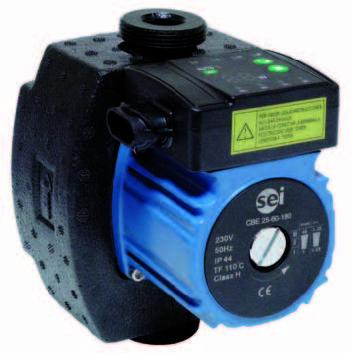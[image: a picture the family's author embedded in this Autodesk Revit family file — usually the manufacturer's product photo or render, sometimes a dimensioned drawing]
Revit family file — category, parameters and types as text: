
# Revit family: CBE_25-60_130-AC52101
name_source: partatom
category: Aparatos eléctricos
revit_build: Autodesk Revit 2016 (Build: 20150220_1215(x64)
units: mm (PartAtom-declared; Revit-internal decimal feet)

## family parameters
Compartido = No
Corte con vacíos al cargar = No
Cota de conector redondo = Diámetro de uso
Mantener orientación de anotación = No
Número OmniClass = 23.80.00.00
Punto de cálculo de habitación = No
Se basa en plano de trabajo = No
Siempre vertical = Sí
Tipo de pieza = Caja de conexiones
Título OmniClass = Electric Power and Lighting

## types (2) — shared parameters
Fabricante = SALVADOR ESCODA
Protección = 6,35 mm (1/4")
URL = www.salvadorescoda.com
zero-valued in all types: Costo

## per-type parameters (varying)
| type | Aislamiento | Caudal | Conexión rácores | Código de montaje | Descripción | Dimensiones Unidad Interior | Imagen de tipo | Modelo | Motor | Máx. presión trabajo | Peso | Presión disponible | Rango temperatura agua | Temperatura ambiente |
| MVD-22T2 | 35 dB(A) |  |  | CL23370 | CONDUCTO BAJA SILUETA | 700 x 210 x 500 mm | <Ninguno> | MVD-22T2/DHN1-DA5 | 521 m3/h | 2,2kW / 39W | 17,5 kg neto |  | 2,6kW / 39W | DC / WZDK100-38GS |
| CBE | 59 dB(A) | 1 m3/h | G1 1/2" DN | AC52101 | BOMBA CIRCULADORA ELECTRONICA CON AISLAMIENTO | 130 x 105 x 100 mm | SEI_CBE.jpg | CBE 25-60_130 | 2 polos, 1x230V - 50Hz | 10 bar | 3,5 Kgs | 5 m.c.a. | 2º a 110 ºC | Hasta 40ºC |
